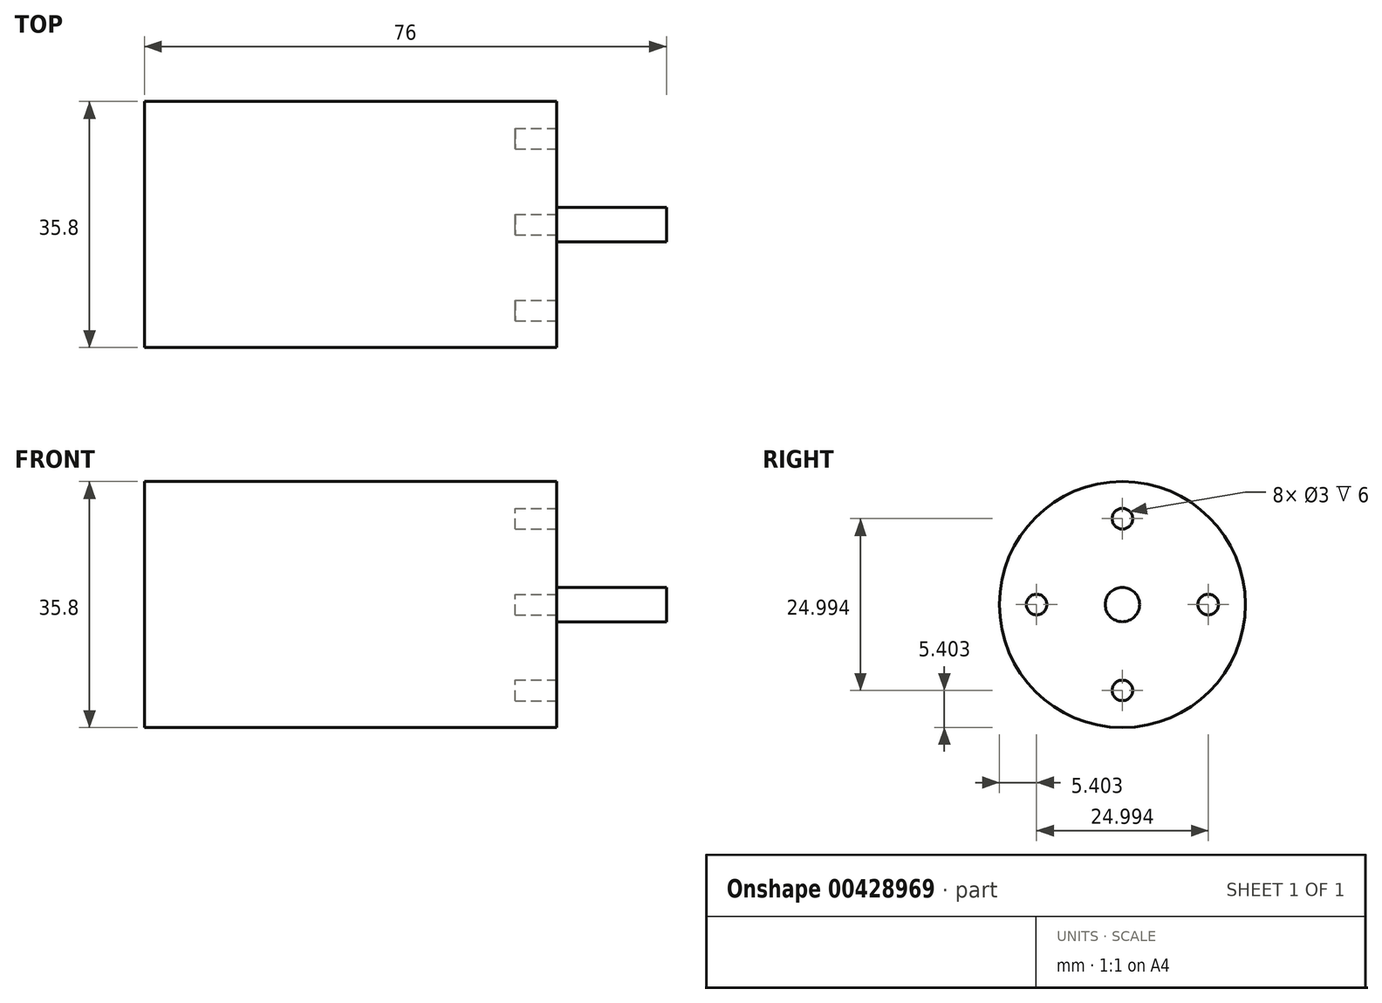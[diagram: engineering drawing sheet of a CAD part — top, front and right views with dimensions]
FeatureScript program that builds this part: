
annotation { "Feature Type Name" : "Feature", "Feature Type Description" : "" }
export const myFeature = defineFeature(function(context is Context, id is Id, definition is map)
    precondition{}
    {
        {
            var Q0;
            Q0=qCreatedBy(makeId("Right.planeOp"),FACE);
            var sketch = newSketch(context, id + "F0", { "sketchPlane" : qUnion([Q0])});
            skCircle(sketch, "E0", {"center": v(0, 0) * mm, "radius": 17.9 * mm});
            skSolve(sketch);
        }
        {
            var Q0;
            Q0=qSketchRegion(id+"F0",true);
            extrude(context, id + "F1", {"entities" : qUnion([Q0]), "endBound" : BoundingType.SYMMETRIC, "depth" : 60 * mm});
        }
        {
            var Q0;
            Q0=makeQuery(id+"F1.opExtrude","CAP_FACE",FACE,{"disambiguationData":[OSD([sQuery(id+"F0.wireOp",EDGE,"E0")])],"isStart":false});
            var sketch = newSketch(context, id + "F2", { "sketchPlane" : qUnion([Q0])});
            skCircle(sketch, "E1", {"center": v(0, 0) * mm, "radius": 2.5 * mm});
            skSolve(sketch);
        }
        {
            var Q0;
            Q0=qSketchRegion(id+"F2",true);
            extrude(context, id + "F3", {"entities" : qUnion([Q0]), "operationType" : NewBodyOperationType.ADD, "depth" : 16 * mm});
        }
        {
            var Q0;
            Q0=makeQuery(id+"F1.opExtrude","CAP_FACE",FACE,{"disambiguationData":[OSD([sQuery(id+"F0.wireOp",EDGE,"E0")])],"isStart":false});
            var sketch = newSketch(context, id + "F4", { "sketchPlane" : qUnion([Q0])});
            skCircle(sketch, "E2", {"center": v(0, 0) * mm, "radius": 12.5 * mm, "construction": true});
            skCircle(sketch, "E3", {"center": v(0, 12.5) * mm, "radius": 1.5 * mm});
            skCircle(sketch, "E4.1.0", {"center": v(-12.5, 0) * mm, "radius": 1.5 * mm});
            skCircle(sketch, "E4.2.0", {"center": v(0, -12.5) * mm, "radius": 1.5 * mm});
            skCircle(sketch, "E4.3.0", {"center": v(12.5, 0) * mm, "radius": 1.5 * mm});
            skSolve(sketch);
        }
        {
            var Q0;
            Q0=qSketchRegion(id+"F4",true);
            extrude(context, id + "F5", {"entities" : qUnion([Q0]), "operationType" : NewBodyOperationType.REMOVE, "oppositeDirection" : true, "depth" : 6 * mm});
        }
        {
            var Q0;
            Q0=makeQuery(id+"F1.opExtrude","SWEPT_BODY",BODY,{"disambiguationData":[OSD([sQuery(id+"F0.wireOp",EDGE,"E0")])]});
            transform(context, id + "F6", {"entities" : qUnion([Q0]), "transformType" : TransformType.TRANSLATION_3D, "dx" : 0 * mm, "dy" : 0 * mm, "dz" : 0 * mm, "makeCopy" : true});
        }
    });
